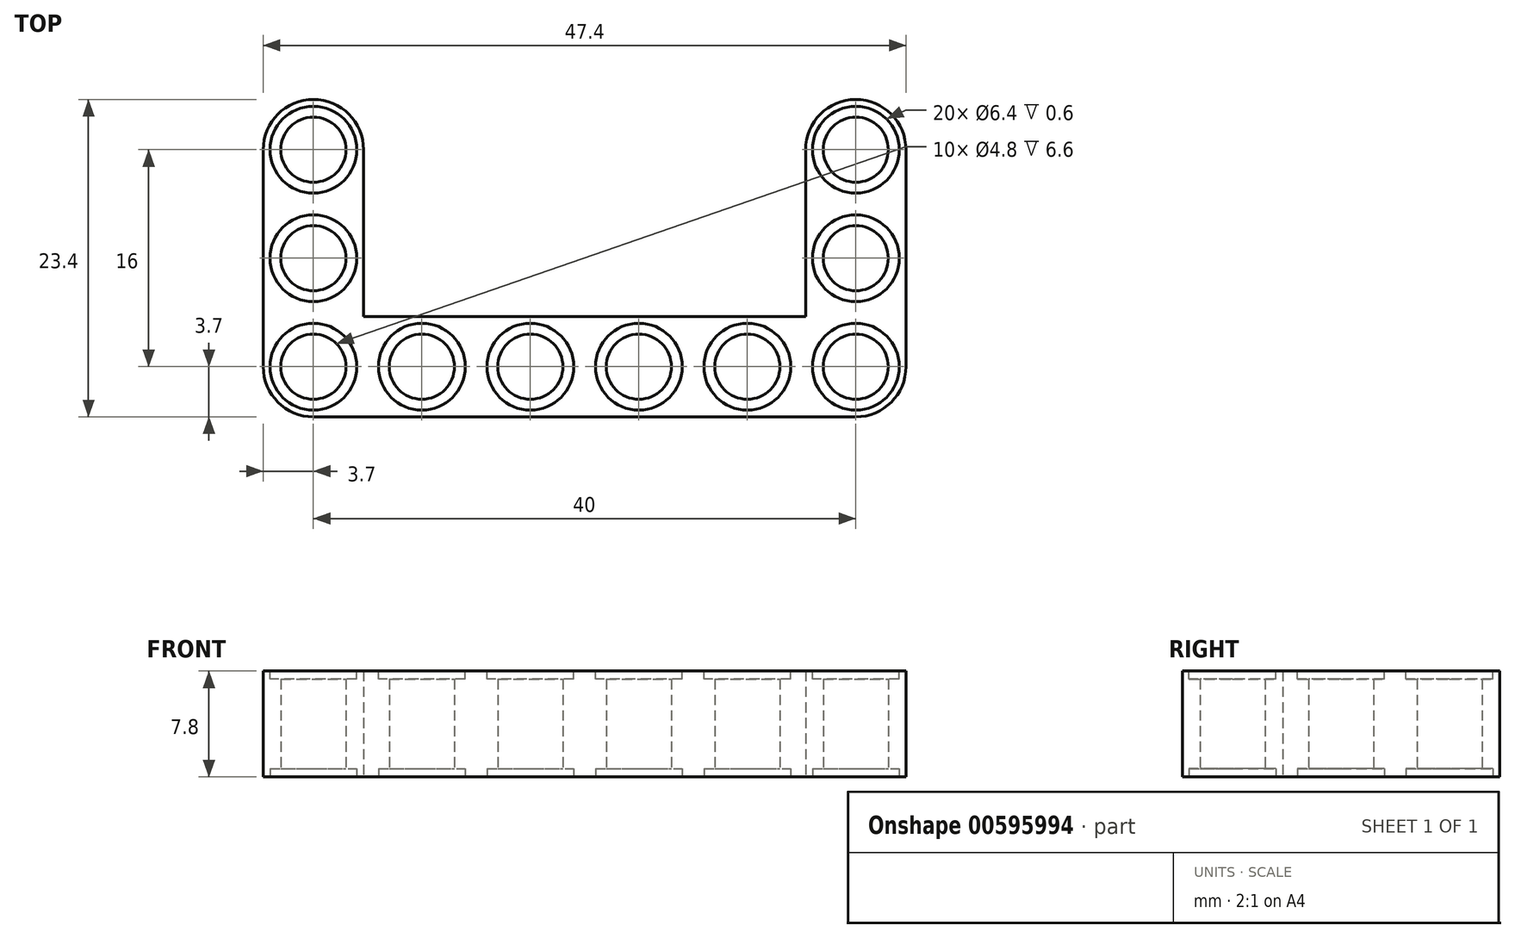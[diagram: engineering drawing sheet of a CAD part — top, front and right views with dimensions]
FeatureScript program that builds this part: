
annotation { "Feature Type Name" : "Feature", "Feature Type Description" : "" }
export const myFeature = defineFeature(function(context is Context, id is Id, definition is map)
    precondition{}
    {
        {
            var Q0;
            Q0=qCreatedBy(makeId("Top.planeOp"),FACE);
            var sketch = newSketch(context, id + "F0", { "sketchPlane" : qUnion([Q0])});
            skLineSegment(sketch, "E0", {"start": v(0, 0) * mm, "end": v(40, 0) * mm});
            skLineSegment(sketch, "E1", {"start": v(3.7, 7.4) * mm, "end": v(40, 7.4) * mm});
            skLineSegment(sketch, "E2", {"start": v(3.7, 7.4) * mm, "end": v(3.7, 19.7) * mm});
            skLineSegment(sketch, "E3", {"start": v(-3.7, 19.7) * mm, "end": v(-3.7, 3.7) * mm});
            skArc(sketch, "E4", {"start": v(0, 0) * mm, "mid": v(-2.62, 1.08) * mm, "end": v(-3.7, 3.7) * mm});
            skArc(sketch, "E5", {"start": v(40, 7.4) * mm, "mid": v(43.7, 3.7) * mm, "end": v(40, 0) * mm});
            skCircle(sketch, "E6", {"center": v(0, 3.7) * mm, "radius": 2.4 * mm});
            skCircle(sketch, "E7.1.0.0", {"center": v(8, 3.7) * mm, "radius": 2.4 * mm});
            skCircle(sketch, "E7.2.0.0", {"center": v(16, 3.7) * mm, "radius": 2.4 * mm});
            skCircle(sketch, "E7.3.0.0", {"center": v(24, 3.7) * mm, "radius": 2.4 * mm});
            skCircle(sketch, "E7.4.0.0", {"center": v(32, 3.7) * mm, "radius": 2.4 * mm});
            skCircle(sketch, "E7.5.0.0", {"center": v(40, 3.7) * mm, "radius": 2.4 * mm});
            skLineSegment(sketch, "E7.direction1", {"start": v(0, 3.7) * mm, "end": v(8, 3.7) * mm, "construction": true});
            skCircle(sketch, "E8.0.1.0", {"center": v(0, 11.7) * mm, "radius": 2.4 * mm});
            skLineSegment(sketch, "E8.direction2", {"start": v(0, 3.7) * mm, "end": v(0, 11.7) * mm, "construction": true});
            skLineSegment(sketch, "E9", {"start": v(20, 0) * mm, "end": v(20, 7.4) * mm, "construction": true});
            skPoint(sketch, "E9.endSnap0", {"position": v(21.85, 7.4) * mm});
            skCircle(sketch, "E10", {"center": v(0, 19.7) * mm, "radius": 2.4 * mm});
            skArc(sketch, "E11", {"start": v(-3.7, 19.7) * mm, "mid": v(0, 23.4) * mm, "end": v(3.7, 19.7) * mm});
            skLineSegment(sketch, "E12.MirrorCS", {"start": v(43.7, 19.7) * mm, "end": v(43.7, 3.7) * mm});
            skLineSegment(sketch, "E13.MirrorCS", {"start": v(36.3, 7.4) * mm, "end": v(36.3, 19.7) * mm});
            skArc(sketch, "E14.MirrorCS", {"start": v(43.7, 19.7) * mm, "mid": v(40, 23.4) * mm, "end": v(36.3, 19.7) * mm});
            skCircle(sketch, "E15.MirrorC", {"center": v(40, 19.7) * mm, "radius": 2.4 * mm});
            skCircle(sketch, "E16.MirrorC", {"center": v(40, 11.7) * mm, "radius": 2.4 * mm});
            skSolve(sketch);
        }
        {
            var Q0;
            Q0 = qSketchRegion(id + "F0", true);
            extrude(context, id + "F1", {"entities" : qUnion([Q0]), "depth" : 7.8 * mm, "offsetDistance" : 25 * mm});
        }
        {
            var Q0;
            Q0=makeQuery(id+"F1.opExtrude","CAP_FACE",FACE,{"disambiguationData":[OSD([sQuery(id+"F0.wireOp",EDGE,"E0"),sQuery(id+"F0.wireOp",EDGE,"E1"),sQuery(id+"F0.wireOp",EDGE,"E2"),sQuery(id+"F0.wireOp",EDGE,"E3"),sQuery(id+"F0.wireOp",EDGE,"E4"),sQuery(id+"F0.wireOp",EDGE,"84a1d7b4-eff3-47ec-896e-d76703566592"),sQuery(id+"F0.wireOp",EDGE,"E5"),sQuery(id+"F0.wireOp",EDGE,"E6"),sQuery(id+"F0.wireOp",EDGE,"E7.1.0.0"),sQuery(id+"F0.wireOp",EDGE,"E7.2.0.0"),sQuery(id+"F0.wireOp",EDGE,"E7.3.0.0"),sQuery(id+"F0.wireOp",EDGE,"E7.4.0.0"),sQuery(id+"F0.wireOp",EDGE,"E7.5.0.0"),sQuery(id+"F0.wireOp",EDGE,"E8.0.1.0"),sQuery(id+"F0.wireOp",EDGE,"7dff2f49-92a3-4902-80ea-11be3855dcdb0.MirrorCS"),sQuery(id+"F0.wireOp",EDGE,"908e048b-6b5c-446e-ad6b-a20ec42be08f0.MirrorCS"),sQuery(id+"F0.wireOp",EDGE,"7aa00db9-4c7a-4d26-bde6-f0bf56d1aef20.MirrorC"),sQuery(id+"F0.wireOp",EDGE,"cb673747-6055-4cbf-bb0b-ce80afeee9330.MirrorCS")])],"isStart":false});
            var sketch = newSketch(context, id + "F2", { "sketchPlane" : qUnion([Q0])});
            skCircle(sketch, "E17.0", {"center": v(0, 3.7) * mm, "radius": 2.4 * mm, "construction": true});
            skCircle(sketch, "E18.0", {"center": v(0, 3.7) * mm, "radius": 3.2 * mm});
            skCircle(sketch, "E19.1.0.0", {"center": v(8, 3.7) * mm, "radius": 3.2 * mm});
            skCircle(sketch, "E19.2.0.0", {"center": v(16, 3.7) * mm, "radius": 3.2 * mm});
            skCircle(sketch, "E19.3.0.0", {"center": v(24, 3.7) * mm, "radius": 3.2 * mm});
            skCircle(sketch, "E19.4.0.0", {"center": v(32, 3.7) * mm, "radius": 3.2 * mm});
            skCircle(sketch, "E19.5.0.0", {"center": v(40, 3.7) * mm, "radius": 3.2 * mm});
            skLineSegment(sketch, "E19.direction1", {"start": v(0, 3.7) * mm, "end": v(8, 3.7) * mm, "construction": true});
            skCircle(sketch, "E20", {"center": v(0, 11.7) * mm, "radius": 3.2 * mm});
            skLineSegment(sketch, "E21", {"start": v(20, 0) * mm, "end": v(20, 7.4) * mm, "construction": true});
            skCircle(sketch, "E22.MirrorC", {"center": v(40, 11.7) * mm, "radius": 3.2 * mm});
            skCircle(sketch, "E23", {"center": v(0, 19.7) * mm, "radius": 3.2 * mm});
            skCircle(sketch, "E24.MirrorC", {"center": v(40, 19.7) * mm, "radius": 3.2 * mm});
            skSolve(sketch);
        }
        {
            var Q0;
            Q0 = qSketchRegion(id + "F2", true);
            extrude(context, id + "F3", {"entities" : qUnion([Q0]), "operationType" : NewBodyOperationType.REMOVE, "oppositeDirection" : true, "depth" : 0.6 * mm, "offsetDistance" : 25 * mm});
        }
        {
            var Q0;
            Q0=makeQuery(id+"F1.opExtrude","CAP_FACE",FACE,{"disambiguationData":[OSD([sQuery(id+"F0.wireOp",EDGE,"E0"),sQuery(id+"F0.wireOp",EDGE,"E1"),sQuery(id+"F0.wireOp",EDGE,"E2"),sQuery(id+"F0.wireOp",EDGE,"E3"),sQuery(id+"F0.wireOp",EDGE,"E4"),sQuery(id+"F0.wireOp",EDGE,"84a1d7b4-eff3-47ec-896e-d76703566592"),sQuery(id+"F0.wireOp",EDGE,"E5"),sQuery(id+"F0.wireOp",EDGE,"E6"),sQuery(id+"F0.wireOp",EDGE,"E7.1.0.0"),sQuery(id+"F0.wireOp",EDGE,"E7.2.0.0"),sQuery(id+"F0.wireOp",EDGE,"E7.3.0.0"),sQuery(id+"F0.wireOp",EDGE,"E7.4.0.0"),sQuery(id+"F0.wireOp",EDGE,"E7.5.0.0"),sQuery(id+"F0.wireOp",EDGE,"E8.0.1.0"),sQuery(id+"F0.wireOp",EDGE,"7dff2f49-92a3-4902-80ea-11be3855dcdb0.MirrorCS"),sQuery(id+"F0.wireOp",EDGE,"908e048b-6b5c-446e-ad6b-a20ec42be08f0.MirrorCS"),sQuery(id+"F0.wireOp",EDGE,"7aa00db9-4c7a-4d26-bde6-f0bf56d1aef20.MirrorC"),sQuery(id+"F0.wireOp",EDGE,"cb673747-6055-4cbf-bb0b-ce80afeee9330.MirrorCS")])],"isStart":true});
            var sketch = newSketch(context, id + "F4", { "sketchPlane" : qUnion([Q0])});
            skCircle(sketch, "E25.0", {"center": v(0, -11.7) * mm, "radius": 3.2 * mm});
            skCircle(sketch, "E26.0", {"center": v(0, -3.7) * mm, "radius": 3.2 * mm});
            skCircle(sketch, "E27.0", {"center": v(8, -3.7) * mm, "radius": 3.2 * mm});
            skCircle(sketch, "E28.0", {"center": v(16, -3.7) * mm, "radius": 3.2 * mm});
            skCircle(sketch, "E29.0", {"center": v(24, -3.7) * mm, "radius": 3.2 * mm});
            skCircle(sketch, "E30.0", {"center": v(32, -3.7) * mm, "radius": 3.2 * mm});
            skCircle(sketch, "E31.0", {"center": v(40, -3.7) * mm, "radius": 3.2 * mm});
            skCircle(sketch, "E32.0", {"center": v(40, -11.7) * mm, "radius": 3.2 * mm});
            skCircle(sketch, "E33.0", {"center": v(0, -19.7) * mm, "radius": 3.2 * mm});
            skCircle(sketch, "E34.0", {"center": v(40, -19.7) * mm, "radius": 3.2 * mm});
            skSolve(sketch);
        }
        {
            var Q0;
            Q0 = qSketchRegion(id + "F4", true);
            extrude(context, id + "F5", {"entities" : qUnion([Q0]), "operationType" : NewBodyOperationType.REMOVE, "oppositeDirection" : true, "depth" : 0.6 * mm, "offsetDistance" : 25 * mm});
        }
    });
